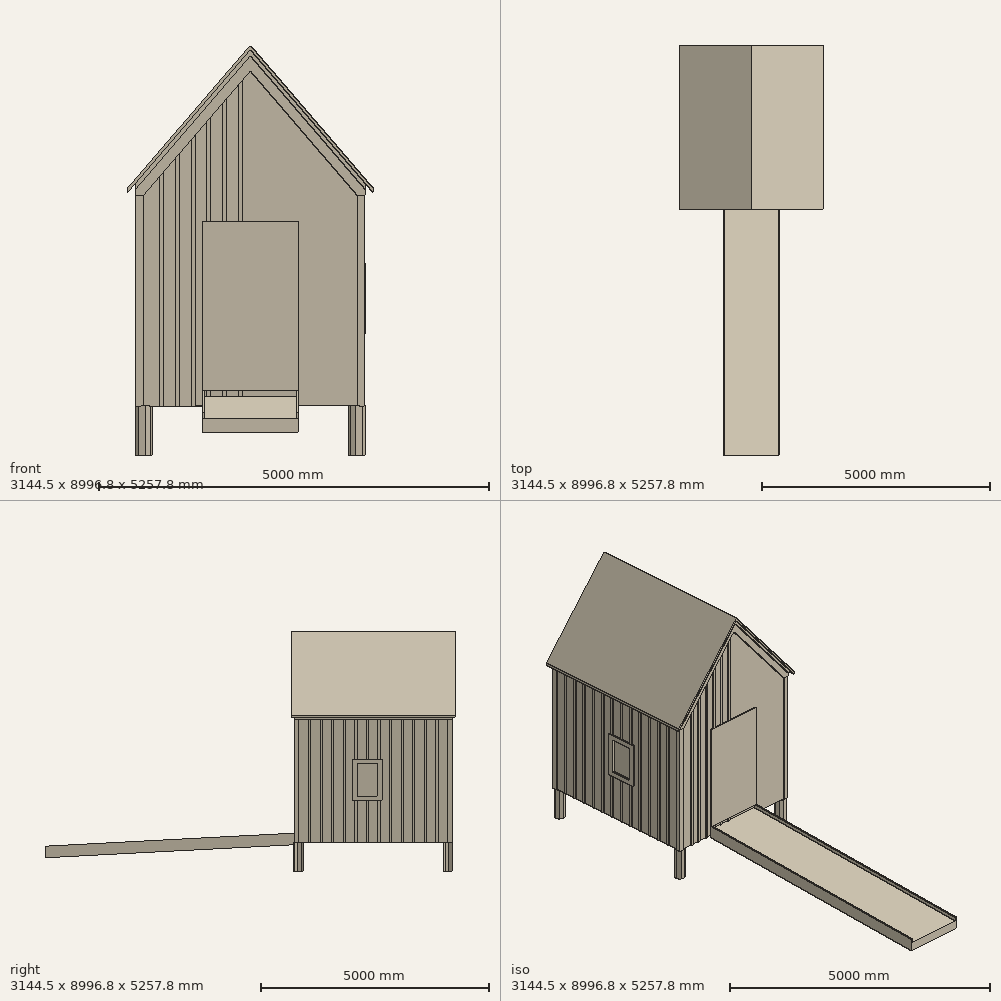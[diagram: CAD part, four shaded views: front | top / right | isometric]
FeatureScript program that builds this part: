
annotation { "Feature Type Name" : "Feature", "Feature Type Description" : "" }
export const myFeature = defineFeature(function(context is Context, id is Id, definition is map)
    precondition{}
    {
        {
            var Q0;
            Q0=qCreatedBy(makeId("Front.planeOp"),FACE);
            var sketch = newSketch(context, id + "F0", { "sketchPlane" : qUnion([Q0])});
            skLineSegment(sketch, "E0", {"start": v(0, 0) * mm, "end": v(0, 2794) * mm});
            skLineSegment(sketch, "E1", {"start": v(0, 2794) * mm, "end": v(1572.26, 4622.8) * mm});
            skLineSegment(sketch, "E2", {"start": v(1572.26, 4622.8) * mm, "end": v(3144.52, 2794) * mm});
            skLineSegment(sketch, "E3", {"start": v(3144.52, 2794) * mm, "end": v(3144.52, 0) * mm});
            skLineSegment(sketch, "E4", {"start": v(3144.52, 0) * mm, "end": v(0, 0) * mm});
            skSolve(sketch);
        }
        {
            var Q0;
            Q0 = qSketchRegion(id + "F0", true);
            extrude(context, id + "F1", {"entities" : qUnion([Q0]), "oppositeDirection" : true, "depth" : 3606.8 * mm});
        }
        {
            var Q0;
            Q0=makeQuery(id+"F1.opExtrude","CAP_FACE",FACE,{"disambiguationData":[OSD([sQuery(id+"F0.wireOp",EDGE,"E0"),sQuery(id+"F0.wireOp",EDGE,"E1"),sQuery(id+"F0.wireOp",EDGE,"E2"),sQuery(id+"F0.wireOp",EDGE,"E3"),sQuery(id+"F0.wireOp",EDGE,"E4")])],"isStart":true});
            var sketch = newSketch(context, id + "F2", { "sketchPlane" : qUnion([Q0])});
            skLineSegment(sketch, "E5", {"start": v(1572.26, 4622.8) * mm, "end": v(1572.26, 2444.29) * mm, "construction": true});
            skLineSegment(sketch, "E6", {"start": v(101.6, 2853.73) * mm, "end": v(101.6, 2701.33) * mm});
            skLineSegment(sketch, "E7", {"start": v(101.6, 2701.33) * mm, "end": v(127, 2701.33) * mm});
            skLineSegment(sketch, "E8", {"start": v(127, 2701.33) * mm, "end": v(127, 0) * mm});
            skPoint(sketch, "E9.orphan", {"position": v(101.6, 0) * mm});
            skLineSegment(sketch, "E10", {"start": v(101.6, 2853.73) * mm, "end": v(0, 2735.56) * mm});
            skLineSegment(sketch, "E11.MirrorCS", {"start": v(3042.92, 2701.33) * mm, "end": v(3017.52, 2701.33) * mm});
            skLineSegment(sketch, "E12.MirrorCS", {"start": v(3042.92, 2853.73) * mm, "end": v(3042.92, 2701.33) * mm});
            skLineSegment(sketch, "E13.MirrorCS", {"start": v(3042.92, 2853.73) * mm, "end": v(3144.52, 2735.56) * mm});
            skLineSegment(sketch, "E14.MirrorCS", {"start": v(3017.52, 2701.33) * mm, "end": v(3017.52, 0) * mm});
            skPoint(sketch, "E15.MirrorP", {"position": v(3042.92, 0) * mm});
            skSolve(sketch);
        }
        {
            var Q0;
            Q0=makeQuery(id+"F2.imprint","IMPRINT",FACE,{"disambiguationData":[TD([[makeQuery(id+"F2.imprint","IMPRINT",EDGE,{"derivedFrom":sQuery(id+"F2.wireOp",EDGE,"E6")}),-1.0]])]});
            var Q1;
            Q1=makeQuery(id+"F2.imprint","IMPRINT",FACE,{"disambiguationData":[TD([[makeQuery(id+"F2.imprint","IMPRINT",EDGE,{"derivedFrom":sQuery(id+"F2.wireOp",EDGE,"E11.MirrorCS")}),1.0]])]});
            extrude(context, id + "F3", {"entities" : qUnion([Q0, Q1]), "operationType" : NewBodyOperationType.REMOVE, "endBound" : BoundingType.THROUGH_ALL, "oppositeDirection" : true, "depth" : 25.4 * mm});
        }
        {
            var Q0;
            Q0=makeQuery(id+"F1.opExtrude","CAP_FACE",FACE,{"disambiguationData":[OSD([sQuery(id+"F0.wireOp",EDGE,"E0"),sQuery(id+"F0.wireOp",EDGE,"E1"),sQuery(id+"F0.wireOp",EDGE,"E2"),sQuery(id+"F0.wireOp",EDGE,"E3"),sQuery(id+"F0.wireOp",EDGE,"E4")])],"isStart":true});
            var sketch = newSketch(context, id + "F4", { "sketchPlane" : qUnion([Q0])});
            skLineSegment(sketch, "E16", {"start": v(101.6, 2853.73) * mm, "end": v(1572.26, 4564.36) * mm});
            skLineSegment(sketch, "E17", {"start": v(1572.26, 4564.36) * mm, "end": v(3042.92, 2853.73) * mm});
            skSolve(sketch);
        }
        {
            var Q0;
            Q0=makeQuery(id+"F4.imprint","IMPRINT",FACE,{"disambiguationData":[TD([[makeQuery(id+"F4.imprint","IMPRINT",EDGE,{"derivedFrom":sQuery(id+"F4.wireOp",EDGE,"E16")}),-1.0]])]});
            extrude(context, id + "F5", {"entities" : qUnion([Q0]), "operationType" : NewBodyOperationType.REMOVE, "oppositeDirection" : true, "depth" : 25.4 * mm});
        }
        {
            var Q0;
            Q0=makeQuery(id+"F1.opExtrude","CAP_FACE",FACE,{"disambiguationData":[OSD([sQuery(id+"F0.wireOp",EDGE,"E0"),sQuery(id+"F0.wireOp",EDGE,"E1"),sQuery(id+"F0.wireOp",EDGE,"E2"),sQuery(id+"F0.wireOp",EDGE,"E3"),sQuery(id+"F0.wireOp",EDGE,"E4")])],"isStart":false});
            var sketch = newSketch(context, id + "F6", { "sketchPlane" : qUnion([Q0])});
            skLineSegment(sketch, "E18.0.0", {"start": v(-1572.26, 4564.36) * mm, "end": v(-101.6, 2853.73) * mm});
            skLineSegment(sketch, "E18.0.1", {"start": v(-101.6, 2853.73) * mm, "end": v(-101.6, 2701.33) * mm});
            skLineSegment(sketch, "E18.0.2", {"start": v(-101.6, 2701.33) * mm, "end": v(-127, 2701.33) * mm});
            skLineSegment(sketch, "E18.0.3", {"start": v(-127, 2701.33) * mm, "end": v(-127, 0) * mm});
            skLineSegment(sketch, "E18.0.4", {"start": v(-127, 0) * mm, "end": v(-3017.52, 0) * mm});
            skLineSegment(sketch, "E18.0.5", {"start": v(-3017.52, 0) * mm, "end": v(-3017.52, 2701.33) * mm});
            skLineSegment(sketch, "E18.0.6", {"start": v(-3017.52, 2701.33) * mm, "end": v(-3042.92, 2701.33) * mm});
            skLineSegment(sketch, "E18.0.7", {"start": v(-3042.92, 2701.33) * mm, "end": v(-3042.92, 2853.73) * mm});
            skLineSegment(sketch, "E18.0.8", {"start": v(-3042.92, 2853.73) * mm, "end": v(-1572.26, 4564.36) * mm});
            skSolve(sketch);
        }
        {
            var Q0;
            Q0 = qSketchRegion(id + "F6", true);
            extrude(context, id + "F7", {"entities" : qUnion([Q0]), "operationType" : NewBodyOperationType.REMOVE, "oppositeDirection" : true, "depth" : 25.4 * mm});
        }
        {
            var Q0;
            Q0=makeQuery(id+"F5.boolean.opBoolean","COPY",FACE,{"derivedFrom":makeQuery(id+"F5.opExtrude","CAP_FACE",FACE,{"disambiguationData":[OSD([sQuery(id+"F0.wireOp",EDGE,"E4"),sQuery(id+"F2.wireOp",EDGE,"E6"),sQuery(id+"F2.wireOp",EDGE,"E7"),sQuery(id+"F2.wireOp",EDGE,"E8"),sQuery(id+"F2.wireOp",EDGE,"E11.MirrorCS"),sQuery(id+"F2.wireOp",EDGE,"E12.MirrorCS"),sQuery(id+"F2.wireOp",EDGE,"E14.MirrorCS"),sQuery(id+"F4.wireOp",EDGE,"E16"),sQuery(id+"F4.wireOp",EDGE,"E17")])],"isStart":false})});
            var sketch = newSketch(context, id + "F8", { "sketchPlane" : qUnion([Q0])});
            skLineSegment(sketch, "E19", {"start": v(101.6, 2775.81) * mm, "end": v(1572.26, 4486.43) * mm});
            skLineSegment(sketch, "E20", {"start": v(1572.26, 4486.43) * mm, "end": v(3042.92, 2775.81) * mm});
            skSolve(sketch);
        }
        {
            var Q0;
            {var subQ3=sQuery(id+"F8.wireOp",EDGE,"E19");Q0=makeQuery(id+"F8.imprint","IMPRINT",FACE,{"disambiguationData":[TD([[makeQuery(id+"F8.imprint","IMPRINT",EDGE,{"derivedFrom":subQ3}),-1.0]])]});}
            extrude(context, id + "F9", {"entities" : qUnion([Q0]), "operationType" : NewBodyOperationType.REMOVE, "oppositeDirection" : true, "depth" : 38.1 * mm});
        }
        {
            var Q0;
            Q0=makeQuery(id+"F7.boolean.opBoolean","COPY",FACE,{"derivedFrom":makeQuery(id+"F7.opExtrude","CAP_FACE",FACE,{"disambiguationData":[OSD([sQuery(id+"F6.wireOp",EDGE,"E18.0.0"),sQuery(id+"F6.wireOp",EDGE,"E18.0.1"),sQuery(id+"F6.wireOp",EDGE,"E18.0.2"),sQuery(id+"F6.wireOp",EDGE,"E18.0.3"),sQuery(id+"F6.wireOp",EDGE,"E18.0.4"),sQuery(id+"F6.wireOp",EDGE,"E18.0.5"),sQuery(id+"F6.wireOp",EDGE,"E18.0.6"),sQuery(id+"F6.wireOp",EDGE,"E18.0.7"),sQuery(id+"F6.wireOp",EDGE,"E18.0.8")])],"isStart":false})});
            var sketch = newSketch(context, id + "F10", { "sketchPlane" : qUnion([Q0])});
            skLineSegment(sketch, "E21.0.0", {"start": v(-1572.26, 4486.43) * mm, "end": v(-101.6, 2775.81) * mm});
            skLineSegment(sketch, "E21.0.1", {"start": v(-101.6, 2775.81) * mm, "end": v(-101.6, 2701.33) * mm});
            skLineSegment(sketch, "E21.0.2", {"start": v(-101.6, 2701.33) * mm, "end": v(-127, 2701.33) * mm});
            skLineSegment(sketch, "E21.0.3", {"start": v(-127, 2701.33) * mm, "end": v(-127, 0) * mm});
            skLineSegment(sketch, "E21.0.4", {"start": v(-127, 0) * mm, "end": v(-3017.52, 0) * mm});
            skLineSegment(sketch, "E21.0.5", {"start": v(-3017.52, 0) * mm, "end": v(-3017.52, 2701.33) * mm});
            skLineSegment(sketch, "E21.0.6", {"start": v(-3017.52, 2701.33) * mm, "end": v(-3042.92, 2701.33) * mm});
            skLineSegment(sketch, "E21.0.7", {"start": v(-3042.92, 2701.33) * mm, "end": v(-3042.92, 2775.81) * mm});
            skLineSegment(sketch, "E21.0.8", {"start": v(-3042.92, 2775.81) * mm, "end": v(-1572.26, 4486.43) * mm});
            skSolve(sketch);
        }
        {
            var Q0;
            Q0 = qSketchRegion(id + "F10", true);
            extrude(context, id + "F11", {"entities" : qUnion([Q0]), "operationType" : NewBodyOperationType.REMOVE, "oppositeDirection" : true, "depth" : 38.1 * mm});
        }
        {
            var Q0;
            Q0=makeQuery(id+"F9.boolean.opBoolean","COPY",FACE,{"derivedFrom":makeQuery(id+"F9.opExtrude","CAP_FACE",FACE,{"disambiguationData":[OSD([sQuery(id+"F0.wireOp",EDGE,"E4"),sQuery(id+"F2.wireOp",EDGE,"E6"),sQuery(id+"F2.wireOp",EDGE,"E7"),sQuery(id+"F2.wireOp",EDGE,"E8"),sQuery(id+"F2.wireOp",EDGE,"E11.MirrorCS"),sQuery(id+"F2.wireOp",EDGE,"E12.MirrorCS"),sQuery(id+"F2.wireOp",EDGE,"E14.MirrorCS"),sQuery(id+"F8.wireOp",EDGE,"E19"),sQuery(id+"F8.wireOp",EDGE,"E20")])],"isStart":false})});
            var sketch = newSketch(context, id + "F12", { "sketchPlane" : qUnion([Q0])});
            skLineSegment(sketch, "E22", {"start": v(127, 2701.33) * mm, "end": v(205.05, 2701.33) * mm});
            skLineSegment(sketch, "E23", {"start": v(205.05, 2701.33) * mm, "end": v(1572.26, 4291.62) * mm});
            skLineSegment(sketch, "E24", {"start": v(1572.26, 4291.62) * mm, "end": v(2939.47, 2701.33) * mm});
            skLineSegment(sketch, "E25", {"start": v(2939.47, 2701.33) * mm, "end": v(3017.52, 2701.33) * mm});
            skSolve(sketch);
        }
        {
            var Q0;
            Q0=makeQuery(id+"F12.imprint","IMPRINT",FACE,{"disambiguationData":[TD([[makeQuery(id+"F12.imprint","IMPRINT",EDGE,{"derivedFrom":sQuery(id+"F12.wireOp",EDGE,"E22")}),-1.0]])]});
            extrude(context, id + "F13", {"entities" : qUnion([Q0]), "operationType" : NewBodyOperationType.REMOVE, "oppositeDirection" : true, "depth" : 25.4 * mm});
        }
        {
            var Q0;
            Q0=makeQuery(id+"F11.boolean.opBoolean","COPY",FACE,{"derivedFrom":makeQuery(id+"F11.opExtrude","CAP_FACE",FACE,{"disambiguationData":[OSD([sQuery(id+"F10.wireOp",EDGE,"E21.0.0"),sQuery(id+"F10.wireOp",EDGE,"E21.0.1"),sQuery(id+"F10.wireOp",EDGE,"E21.0.2"),sQuery(id+"F10.wireOp",EDGE,"E21.0.3"),sQuery(id+"F10.wireOp",EDGE,"E21.0.4"),sQuery(id+"F10.wireOp",EDGE,"E21.0.5"),sQuery(id+"F10.wireOp",EDGE,"E21.0.6"),sQuery(id+"F10.wireOp",EDGE,"E21.0.7"),sQuery(id+"F10.wireOp",EDGE,"E21.0.8")])],"isStart":false})});
            var sketch = newSketch(context, id + "F14", { "sketchPlane" : qUnion([Q0])});
            skLineSegment(sketch, "E26.0.0", {"start": v(-205.05, 2701.33) * mm, "end": v(-127, 2701.33) * mm});
            skLineSegment(sketch, "E26.0.1", {"start": v(-127, 2701.33) * mm, "end": v(-127, 0) * mm});
            skLineSegment(sketch, "E26.0.2", {"start": v(-127, 0) * mm, "end": v(-3017.52, 0) * mm});
            skLineSegment(sketch, "E26.0.3", {"start": v(-3017.52, 0) * mm, "end": v(-3017.52, 2701.33) * mm});
            skLineSegment(sketch, "E26.0.4", {"start": v(-3017.52, 2701.33) * mm, "end": v(-2939.47, 2701.33) * mm});
            skLineSegment(sketch, "E26.0.5", {"start": v(-2939.47, 2701.33) * mm, "end": v(-1572.26, 4291.62) * mm});
            skLineSegment(sketch, "E26.0.6", {"start": v(-1572.26, 4291.62) * mm, "end": v(-205.05, 2701.33) * mm});
            skSolve(sketch);
        }
        {
            var Q0;
            Q0 = qSketchRegion(id + "F14", true);
            extrude(context, id + "F15", {"entities" : qUnion([Q0]), "operationType" : NewBodyOperationType.REMOVE, "oppositeDirection" : true, "depth" : 25.4 * mm});
        }
        {
            var Q0;
            Q0=makeQuery(id+"F1.opExtrude","SWEPT_FACE",FACE,{"disambiguationData":[OSD([sQuery(id+"F0.wireOp",EDGE,"E4")])]});
            var sketch = newSketch(context, id + "F16", { "sketchPlane" : qUnion([Q0])});
            skLineSegment(sketch, "E27.bottom", {"start": v(99.06, -66.04) * mm, "end": v(200.66, -66.04) * mm});
            skLineSegment(sketch, "E27.top", {"start": v(99.06, -167.64) * mm, "end": v(200.66, -167.64) * mm});
            skLineSegment(sketch, "E27.left", {"start": v(99.06, -66.04) * mm, "end": v(99.06, -167.64) * mm});
            skLineSegment(sketch, "E27.right", {"start": v(200.66, -66.04) * mm, "end": v(200.66, -167.64) * mm});
            skLineSegment(sketch, "E28.bottom", {"start": v(99.06, -3540.76) * mm, "end": v(200.66, -3540.76) * mm});
            skLineSegment(sketch, "E28.top", {"start": v(99.06, -3439.16) * mm, "end": v(200.66, -3439.16) * mm});
            skLineSegment(sketch, "E28.left", {"start": v(99.06, -3540.76) * mm, "end": v(99.06, -3439.16) * mm});
            skLineSegment(sketch, "E28.right", {"start": v(200.66, -3540.76) * mm, "end": v(200.66, -3439.16) * mm});
            skLineSegment(sketch, "E29.bottom", {"start": v(3040.38, -3540.76) * mm, "end": v(2938.78, -3540.76) * mm});
            skLineSegment(sketch, "E29.top", {"start": v(3040.38, -3439.16) * mm, "end": v(2938.78, -3439.16) * mm});
            skLineSegment(sketch, "E29.left", {"start": v(3040.38, -3540.76) * mm, "end": v(3040.38, -3439.16) * mm});
            skLineSegment(sketch, "E29.right", {"start": v(2938.78, -3540.76) * mm, "end": v(2938.78, -3439.16) * mm});
            skLineSegment(sketch, "E30.bottom", {"start": v(3040.38, -66.04) * mm, "end": v(2938.78, -66.04) * mm});
            skLineSegment(sketch, "E30.top", {"start": v(3040.38, -167.64) * mm, "end": v(2938.78, -167.64) * mm});
            skLineSegment(sketch, "E30.left", {"start": v(3040.38, -66.04) * mm, "end": v(3040.38, -167.64) * mm});
            skLineSegment(sketch, "E30.right", {"start": v(2938.78, -66.04) * mm, "end": v(2938.78, -167.64) * mm});
            skSolve(sketch);
        }
        {
            var Q0;
            Q0 = qSketchRegion(id + "F16", true);
            var Q1;
            Q1=makeQuery(id+"F15.boolean.opBoolean","MERGE",FACE,{"derivedFrom":[makeQuery(id+"F13.boolean.opBoolean","MERGE",FACE,{"derivedFrom":[makeQuery(id+"F3.boolean.opBoolean","COPY",FACE,{"derivedFrom":makeQuery(id+"F3.opExtrude","SWEPT_FACE",FACE,{"disambiguationData":[OSD([sQuery(id+"F2.wireOp",EDGE,"E11.MirrorCS")])]})}),makeQuery(id+"F13.opExtrude","SWEPT_FACE",FACE,{"disambiguationData":[OSD([sQuery(id+"F12.wireOp",EDGE,"E25")])]})]}),makeQuery(id+"F15.opExtrude","SWEPT_FACE",FACE,{"disambiguationData":[OSD([sQuery(id+"F14.wireOp",EDGE,"E26.0.4")])]})]});
            extrude(context, id + "F17", {"entities" : qUnion([Q0]), "operationType" : NewBodyOperationType.ADD, "endBound" : BoundingType.UP_TO_SURFACE, "oppositeDirection" : true, "endBoundEntityFace" : qUnion([Q1]), "depth" : 25.4 * mm});
        }
        {
            var Q0;
            Q0=makeQuery(id+"F17.boolean.opBoolean","MERGE",FACE,{"derivedFrom":[makeQuery(id+"F1.opExtrude","SWEPT_FACE",FACE,{"disambiguationData":[OSD([sQuery(id+"F0.wireOp",EDGE,"E4")])]}),makeQuery(id+"F17.opExtrude","CAP_FACE",FACE,{"disambiguationData":[OSD([sQuery(id+"F16.wireOp",EDGE,"E27.bottom"),sQuery(id+"F16.wireOp",EDGE,"E27.top"),sQuery(id+"F16.wireOp",EDGE,"E27.left"),sQuery(id+"F16.wireOp",EDGE,"E27.right")])],"isStart":true}),makeQuery(id+"F17.opExtrude","CAP_FACE",FACE,{"disambiguationData":[OSD([sQuery(id+"F16.wireOp",EDGE,"E28.bottom"),sQuery(id+"F16.wireOp",EDGE,"E28.top"),sQuery(id+"F16.wireOp",EDGE,"E28.left"),sQuery(id+"F16.wireOp",EDGE,"E28.right")])],"isStart":true}),makeQuery(id+"F17.opExtrude","CAP_FACE",FACE,{"disambiguationData":[OSD([sQuery(id+"F16.wireOp",EDGE,"E29.bottom"),sQuery(id+"F16.wireOp",EDGE,"E29.top"),sQuery(id+"F16.wireOp",EDGE,"E29.left"),sQuery(id+"F16.wireOp",EDGE,"E29.right")])],"isStart":true}),makeQuery(id+"F17.opExtrude","CAP_FACE",FACE,{"disambiguationData":[OSD([sQuery(id+"F16.wireOp",EDGE,"E30.bottom"),sQuery(id+"F16.wireOp",EDGE,"E30.top"),sQuery(id+"F16.wireOp",EDGE,"E30.left"),sQuery(id+"F16.wireOp",EDGE,"E30.right")])],"isStart":true})]});
            var sketch = newSketch(context, id + "F18", { "sketchPlane" : qUnion([Q0])});
            skLineSegment(sketch, "E31.bottom", {"start": v(104.14, -3175) * mm, "end": v(127, -3175) * mm});
            skLineSegment(sketch, "E31.top", {"start": v(104.14, -3225.8) * mm, "end": v(127, -3225.8) * mm});
            skLineSegment(sketch, "E31.left", {"start": v(104.14, -3175) * mm, "end": v(104.14, -3225.8) * mm});
            skLineSegment(sketch, "E31.right", {"start": v(127, -3175) * mm, "end": v(127, -3225.8) * mm});
            skLineSegment(sketch, "E32.0.1.0", {"start": v(104.14, -2971.8) * mm, "end": v(127, -2971.8) * mm});
            skLineSegment(sketch, "E32.0.1.1", {"start": v(127, -2921) * mm, "end": v(127, -2971.8) * mm});
            skLineSegment(sketch, "E32.0.1.2", {"start": v(104.14, -2921) * mm, "end": v(127, -2921) * mm});
            skLineSegment(sketch, "E32.0.1.3", {"start": v(104.14, -2921) * mm, "end": v(104.14, -2971.8) * mm});
            skLineSegment(sketch, "E32.0.2.0", {"start": v(104.14, -2717.8) * mm, "end": v(127, -2717.8) * mm});
            skLineSegment(sketch, "E32.0.2.1", {"start": v(127, -2667) * mm, "end": v(127, -2717.8) * mm});
            skLineSegment(sketch, "E32.0.2.2", {"start": v(104.14, -2667) * mm, "end": v(127, -2667) * mm});
            skLineSegment(sketch, "E32.0.2.3", {"start": v(104.14, -2667) * mm, "end": v(104.14, -2717.8) * mm});
            skLineSegment(sketch, "E32.0.3.0", {"start": v(104.14, -2463.8) * mm, "end": v(127, -2463.8) * mm});
            skLineSegment(sketch, "E32.0.3.1", {"start": v(127, -2413) * mm, "end": v(127, -2463.8) * mm});
            skLineSegment(sketch, "E32.0.3.2", {"start": v(104.14, -2413) * mm, "end": v(127, -2413) * mm});
            skLineSegment(sketch, "E32.0.3.3", {"start": v(104.14, -2413) * mm, "end": v(104.14, -2463.8) * mm});
            skLineSegment(sketch, "E32.0.4.0", {"start": v(104.14, -2209.8) * mm, "end": v(127, -2209.8) * mm});
            skLineSegment(sketch, "E32.0.4.1", {"start": v(127, -2159) * mm, "end": v(127, -2209.8) * mm});
            skLineSegment(sketch, "E32.0.4.2", {"start": v(104.14, -2159) * mm, "end": v(127, -2159) * mm});
            skLineSegment(sketch, "E32.0.4.3", {"start": v(104.14, -2159) * mm, "end": v(104.14, -2209.8) * mm});
            skLineSegment(sketch, "E32.0.5.0", {"start": v(104.14, -1955.8) * mm, "end": v(127, -1955.8) * mm});
            skLineSegment(sketch, "E32.0.5.1", {"start": v(127, -1905) * mm, "end": v(127, -1955.8) * mm});
            skLineSegment(sketch, "E32.0.5.2", {"start": v(104.14, -1905) * mm, "end": v(127, -1905) * mm});
            skLineSegment(sketch, "E32.0.5.3", {"start": v(104.14, -1905) * mm, "end": v(104.14, -1955.8) * mm});
            skLineSegment(sketch, "E32.0.6.0", {"start": v(104.14, -1701.8) * mm, "end": v(127, -1701.8) * mm});
            skLineSegment(sketch, "E32.0.6.1", {"start": v(127, -1651) * mm, "end": v(127, -1701.8) * mm});
            skLineSegment(sketch, "E32.0.6.2", {"start": v(104.14, -1651) * mm, "end": v(127, -1651) * mm});
            skLineSegment(sketch, "E32.0.6.3", {"start": v(104.14, -1651) * mm, "end": v(104.14, -1701.8) * mm});
            skLineSegment(sketch, "E32.0.7.0", {"start": v(104.14, -1447.8) * mm, "end": v(127, -1447.8) * mm});
            skLineSegment(sketch, "E32.0.7.1", {"start": v(127, -1397) * mm, "end": v(127, -1447.8) * mm});
            skLineSegment(sketch, "E32.0.7.2", {"start": v(104.14, -1397) * mm, "end": v(127, -1397) * mm});
            skLineSegment(sketch, "E32.0.7.3", {"start": v(104.14, -1397) * mm, "end": v(104.14, -1447.8) * mm});
            skLineSegment(sketch, "E32.0.8.0", {"start": v(104.14, -1193.8) * mm, "end": v(127, -1193.8) * mm});
            skLineSegment(sketch, "E32.0.8.1", {"start": v(127, -1143) * mm, "end": v(127, -1193.8) * mm});
            skLineSegment(sketch, "E32.0.8.2", {"start": v(104.14, -1143) * mm, "end": v(127, -1143) * mm});
            skLineSegment(sketch, "E32.0.8.3", {"start": v(104.14, -1143) * mm, "end": v(104.14, -1193.8) * mm});
            skLineSegment(sketch, "E32.0.9.0", {"start": v(104.14, -939.8) * mm, "end": v(127, -939.8) * mm});
            skLineSegment(sketch, "E32.0.9.1", {"start": v(127, -889) * mm, "end": v(127, -939.8) * mm});
            skLineSegment(sketch, "E32.0.9.2", {"start": v(104.14, -889) * mm, "end": v(127, -889) * mm});
            skLineSegment(sketch, "E32.0.9.3", {"start": v(104.14, -889) * mm, "end": v(104.14, -939.8) * mm});
            skLineSegment(sketch, "E32.0.10.0", {"start": v(104.14, -685.8) * mm, "end": v(127, -685.8) * mm});
            skLineSegment(sketch, "E32.0.10.1", {"start": v(127, -635) * mm, "end": v(127, -685.8) * mm});
            skLineSegment(sketch, "E32.0.10.2", {"start": v(104.14, -635) * mm, "end": v(127, -635) * mm});
            skLineSegment(sketch, "E32.0.10.3", {"start": v(104.14, -635) * mm, "end": v(104.14, -685.8) * mm});
            skLineSegment(sketch, "E32.0.11.0", {"start": v(104.14, -431.8) * mm, "end": v(127, -431.8) * mm});
            skLineSegment(sketch, "E32.0.11.1", {"start": v(127, -381) * mm, "end": v(127, -431.8) * mm});
            skLineSegment(sketch, "E32.0.11.2", {"start": v(104.14, -381) * mm, "end": v(127, -381) * mm});
            skLineSegment(sketch, "E32.0.11.3", {"start": v(104.14, -381) * mm, "end": v(104.14, -431.8) * mm});
            skLineSegment(sketch, "E32.1.0.0", {"start": v(3017.52, -3225.8) * mm, "end": v(3040.38, -3225.8) * mm});
            skLineSegment(sketch, "E32.1.0.1", {"start": v(3040.38, -3175) * mm, "end": v(3040.38, -3225.8) * mm});
            skLineSegment(sketch, "E32.1.0.2", {"start": v(3017.52, -3175) * mm, "end": v(3040.38, -3175) * mm});
            skLineSegment(sketch, "E32.1.0.3", {"start": v(3017.52, -3175) * mm, "end": v(3017.52, -3225.8) * mm});
            skLineSegment(sketch, "E32.1.1.0", {"start": v(3017.52, -2971.8) * mm, "end": v(3040.38, -2971.8) * mm});
            skLineSegment(sketch, "E32.1.1.1", {"start": v(3040.38, -2921) * mm, "end": v(3040.38, -2971.8) * mm});
            skLineSegment(sketch, "E32.1.1.2", {"start": v(3017.52, -2921) * mm, "end": v(3040.38, -2921) * mm});
            skLineSegment(sketch, "E32.1.1.3", {"start": v(3017.52, -2921) * mm, "end": v(3017.52, -2971.8) * mm});
            skLineSegment(sketch, "E32.1.2.0", {"start": v(3017.52, -2717.8) * mm, "end": v(3040.38, -2717.8) * mm});
            skLineSegment(sketch, "E32.1.2.1", {"start": v(3040.38, -2667) * mm, "end": v(3040.38, -2717.8) * mm});
            skLineSegment(sketch, "E32.1.2.2", {"start": v(3017.52, -2667) * mm, "end": v(3040.38, -2667) * mm});
            skLineSegment(sketch, "E32.1.2.3", {"start": v(3017.52, -2667) * mm, "end": v(3017.52, -2717.8) * mm});
            skLineSegment(sketch, "E32.1.3.0", {"start": v(3017.52, -2463.8) * mm, "end": v(3040.38, -2463.8) * mm});
            skLineSegment(sketch, "E32.1.3.1", {"start": v(3040.38, -2413) * mm, "end": v(3040.38, -2463.8) * mm});
            skLineSegment(sketch, "E32.1.3.2", {"start": v(3017.52, -2413) * mm, "end": v(3040.38, -2413) * mm});
            skLineSegment(sketch, "E32.1.3.3", {"start": v(3017.52, -2413) * mm, "end": v(3017.52, -2463.8) * mm});
            skLineSegment(sketch, "E32.1.4.0", {"start": v(3017.52, -2209.8) * mm, "end": v(3040.38, -2209.8) * mm});
            skLineSegment(sketch, "E32.1.4.1", {"start": v(3040.38, -2159) * mm, "end": v(3040.38, -2209.8) * mm});
            skLineSegment(sketch, "E32.1.4.2", {"start": v(3017.52, -2159) * mm, "end": v(3040.38, -2159) * mm});
            skLineSegment(sketch, "E32.1.4.3", {"start": v(3017.52, -2159) * mm, "end": v(3017.52, -2209.8) * mm});
            skLineSegment(sketch, "E32.1.5.0", {"start": v(3017.52, -1955.8) * mm, "end": v(3040.38, -1955.8) * mm});
            skLineSegment(sketch, "E32.1.5.1", {"start": v(3040.38, -1905) * mm, "end": v(3040.38, -1955.8) * mm});
            skLineSegment(sketch, "E32.1.5.2", {"start": v(3017.52, -1905) * mm, "end": v(3040.38, -1905) * mm});
            skLineSegment(sketch, "E32.1.5.3", {"start": v(3017.52, -1905) * mm, "end": v(3017.52, -1955.8) * mm});
            skLineSegment(sketch, "E32.1.6.0", {"start": v(3017.52, -1701.8) * mm, "end": v(3040.38, -1701.8) * mm});
            skLineSegment(sketch, "E32.1.6.1", {"start": v(3040.38, -1651) * mm, "end": v(3040.38, -1701.8) * mm});
            skLineSegment(sketch, "E32.1.6.2", {"start": v(3017.52, -1651) * mm, "end": v(3040.38, -1651) * mm});
            skLineSegment(sketch, "E32.1.6.3", {"start": v(3017.52, -1651) * mm, "end": v(3017.52, -1701.8) * mm});
            skLineSegment(sketch, "E32.1.7.0", {"start": v(3017.52, -1447.8) * mm, "end": v(3040.38, -1447.8) * mm});
            skLineSegment(sketch, "E32.1.7.1", {"start": v(3040.38, -1397) * mm, "end": v(3040.38, -1447.8) * mm});
            skLineSegment(sketch, "E32.1.7.2", {"start": v(3017.52, -1397) * mm, "end": v(3040.38, -1397) * mm});
            skLineSegment(sketch, "E32.1.7.3", {"start": v(3017.52, -1397) * mm, "end": v(3017.52, -1447.8) * mm});
            skLineSegment(sketch, "E32.1.8.0", {"start": v(3017.52, -1193.8) * mm, "end": v(3040.38, -1193.8) * mm});
            skLineSegment(sketch, "E32.1.8.1", {"start": v(3040.38, -1143) * mm, "end": v(3040.38, -1193.8) * mm});
            skLineSegment(sketch, "E32.1.8.2", {"start": v(3017.52, -1143) * mm, "end": v(3040.38, -1143) * mm});
            skLineSegment(sketch, "E32.1.8.3", {"start": v(3017.52, -1143) * mm, "end": v(3017.52, -1193.8) * mm});
            skLineSegment(sketch, "E32.1.9.0", {"start": v(3017.52, -939.8) * mm, "end": v(3040.38, -939.8) * mm});
            skLineSegment(sketch, "E32.1.9.1", {"start": v(3040.38, -889) * mm, "end": v(3040.38, -939.8) * mm});
            skLineSegment(sketch, "E32.1.9.2", {"start": v(3017.52, -889) * mm, "end": v(3040.38, -889) * mm});
            skLineSegment(sketch, "E32.1.9.3", {"start": v(3017.52, -889) * mm, "end": v(3017.52, -939.8) * mm});
            skLineSegment(sketch, "E32.1.10.0", {"start": v(3017.52, -685.8) * mm, "end": v(3040.38, -685.8) * mm});
            skLineSegment(sketch, "E32.1.10.1", {"start": v(3040.38, -635) * mm, "end": v(3040.38, -685.8) * mm});
            skLineSegment(sketch, "E32.1.10.2", {"start": v(3017.52, -635) * mm, "end": v(3040.38, -635) * mm});
            skLineSegment(sketch, "E32.1.10.3", {"start": v(3017.52, -635) * mm, "end": v(3017.52, -685.8) * mm});
            skLineSegment(sketch, "E32.1.11.0", {"start": v(3017.52, -431.8) * mm, "end": v(3040.38, -431.8) * mm});
            skLineSegment(sketch, "E32.1.11.1", {"start": v(3040.38, -381) * mm, "end": v(3040.38, -431.8) * mm});
            skLineSegment(sketch, "E32.1.11.2", {"start": v(3017.52, -381) * mm, "end": v(3040.38, -381) * mm});
            skLineSegment(sketch, "E32.1.11.3", {"start": v(3017.52, -381) * mm, "end": v(3017.52, -431.8) * mm});
            skLineSegment(sketch, "E32.direction1", {"start": v(104.14, -3225.8) * mm, "end": v(3017.52, -3225.8) * mm, "construction": true});
            skLineSegment(sketch, "E32.direction2", {"start": v(104.14, -3225.8) * mm, "end": v(104.14, -2971.8) * mm, "construction": true});
            skSolve(sketch);
        }
        {
            var Q0;
            Q0 = qSketchRegion(id + "F18", true);
            var Q1;
            Q1=makeQuery(id+"F15.boolean.opBoolean","MERGE",FACE,{"derivedFrom":[makeQuery(id+"F13.boolean.opBoolean","MERGE",FACE,{"derivedFrom":[makeQuery(id+"F3.boolean.opBoolean","COPY",FACE,{"derivedFrom":makeQuery(id+"F3.opExtrude","SWEPT_FACE",FACE,{"disambiguationData":[OSD([sQuery(id+"F2.wireOp",EDGE,"E11.MirrorCS")])]})}),makeQuery(id+"F13.opExtrude","SWEPT_FACE",FACE,{"disambiguationData":[OSD([sQuery(id+"F12.wireOp",EDGE,"E25")])]})]}),makeQuery(id+"F15.opExtrude","SWEPT_FACE",FACE,{"disambiguationData":[OSD([sQuery(id+"F14.wireOp",EDGE,"E26.0.4")])]})]});
            extrude(context, id + "F19", {"entities" : qUnion([Q0]), "operationType" : NewBodyOperationType.ADD, "endBound" : BoundingType.UP_TO_SURFACE, "oppositeDirection" : true, "endBoundEntityFace" : qUnion([Q1]), "depth" : 25.4 * mm});
        }
        {
            var Q0;
            Q0=makeQuery(id+"F19.boolean.opBoolean","MERGE",FACE,{"derivedFrom":[makeQuery(id+"F17.boolean.opBoolean","MERGE",FACE,{"derivedFrom":[makeQuery(id+"F1.opExtrude","SWEPT_FACE",FACE,{"disambiguationData":[OSD([sQuery(id+"F0.wireOp",EDGE,"E4")])]}),makeQuery(id+"F17.opExtrude","CAP_FACE",FACE,{"disambiguationData":[OSD([sQuery(id+"F16.wireOp",EDGE,"E27.bottom"),sQuery(id+"F16.wireOp",EDGE,"E27.top"),sQuery(id+"F16.wireOp",EDGE,"E27.left"),sQuery(id+"F16.wireOp",EDGE,"E27.right")])],"isStart":true}),makeQuery(id+"F17.opExtrude","CAP_FACE",FACE,{"disambiguationData":[OSD([sQuery(id+"F16.wireOp",EDGE,"E28.bottom"),sQuery(id+"F16.wireOp",EDGE,"E28.top"),sQuery(id+"F16.wireOp",EDGE,"E28.left"),sQuery(id+"F16.wireOp",EDGE,"E28.right")])],"isStart":true}),makeQuery(id+"F17.opExtrude","CAP_FACE",FACE,{"disambiguationData":[OSD([sQuery(id+"F16.wireOp",EDGE,"E29.bottom"),sQuery(id+"F16.wireOp",EDGE,"E29.top"),sQuery(id+"F16.wireOp",EDGE,"E29.left"),sQuery(id+"F16.wireOp",EDGE,"E29.right")])],"isStart":true}),makeQuery(id+"F17.opExtrude","CAP_FACE",FACE,{"disambiguationData":[OSD([sQuery(id+"F16.wireOp",EDGE,"E30.bottom"),sQuery(id+"F16.wireOp",EDGE,"E30.top"),sQuery(id+"F16.wireOp",EDGE,"E30.left"),sQuery(id+"F16.wireOp",EDGE,"E30.right")])],"isStart":true})]}),makeQuery(id+"F19.opExtrude","CAP_FACE",FACE,{"disambiguationData":[OSD([sQuery(id+"F18.wireOp",EDGE,"E31.bottom"),sQuery(id+"F18.wireOp",EDGE,"E31.top"),sQuery(id+"F18.wireOp",EDGE,"E31.left"),sQuery(id+"F18.wireOp",EDGE,"E31.right")])],"isStart":true}),makeQuery(id+"F19.opExtrude","CAP_FACE",FACE,{"disambiguationData":[OSD([sQuery(id+"F18.wireOp",EDGE,"E32.0.1.0"),sQuery(id+"F18.wireOp",EDGE,"E32.0.1.1"),sQuery(id+"F18.wireOp",EDGE,"E32.0.1.2"),sQuery(id+"F18.wireOp",EDGE,"E32.0.1.3")])],"isStart":true}),makeQuery(id+"F19.opExtrude","CAP_FACE",FACE,{"disambiguationData":[OSD([sQuery(id+"F18.wireOp",EDGE,"E32.0.2.0"),sQuery(id+"F18.wireOp",EDGE,"E32.0.2.1"),sQuery(id+"F18.wireOp",EDGE,"E32.0.2.2"),sQuery(id+"F18.wireOp",EDGE,"E32.0.2.3")])],"isStart":true}),makeQuery(id+"F19.opExtrude","CAP_FACE",FACE,{"disambiguationData":[OSD([sQuery(id+"F18.wireOp",EDGE,"E32.0.3.0"),sQuery(id+"F18.wireOp",EDGE,"E32.0.3.1"),sQuery(id+"F18.wireOp",EDGE,"E32.0.3.2"),sQuery(id+"F18.wireOp",EDGE,"E32.0.3.3")])],"isStart":true}),makeQuery(id+"F19.opExtrude","CAP_FACE",FACE,{"disambiguationData":[OSD([sQuery(id+"F18.wireOp",EDGE,"E32.0.4.0"),sQuery(id+"F18.wireOp",EDGE,"E32.0.4.1"),sQuery(id+"F18.wireOp",EDGE,"E32.0.4.2"),sQuery(id+"F18.wireOp",EDGE,"E32.0.4.3")])],"isStart":true}),makeQuery(id+"F19.opExtrude","CAP_FACE",FACE,{"disambiguationData":[OSD([sQuery(id+"F18.wireOp",EDGE,"E32.0.5.0"),sQuery(id+"F18.wireOp",EDGE,"E32.0.5.1"),sQuery(id+"F18.wireOp",EDGE,"E32.0.5.2"),sQuery(id+"F18.wireOp",EDGE,"E32.0.5.3")])],"isStart":true}),makeQuery(id+"F19.opExtrude","CAP_FACE",FACE,{"disambiguationData":[OSD([sQuery(id+"F18.wireOp",EDGE,"E32.0.6.0"),sQuery(id+"F18.wireOp",EDGE,"E32.0.6.1"),sQuery(id+"F18.wireOp",EDGE,"E32.0.6.2"),sQuery(id+"F18.wireOp",EDGE,"E32.0.6.3")])],"isStart":true}),makeQuery(id+"F19.opExtrude","CAP_FACE",FACE,{"disambiguationData":[OSD([sQuery(id+"F18.wireOp",EDGE,"E32.0.7.0"),sQuery(id+"F18.wireOp",EDGE,"E32.0.7.1"),sQuery(id+"F18.wireOp",EDGE,"E32.0.7.2"),sQuery(id+"F18.wireOp",EDGE,"E32.0.7.3")])],"isStart":true}),makeQuery(id+"F19.opExtrude","CAP_FACE",FACE,{"disambiguationData":[OSD([sQuery(id+"F18.wireOp",EDGE,"E32.0.8.0"),sQuery(id+"F18.wireOp",EDGE,"E32.0.8.1"),sQuery(id+"F18.wireOp",EDGE,"E32.0.8.2"),sQuery(id+"F18.wireOp",EDGE,"E32.0.8.3")])],"isStart":true}),makeQuery(id+"F19.opExtrude","CAP_FACE",FACE,{"disambiguationData":[OSD([sQuery(id+"F18.wireOp",EDGE,"E32.0.9.0"),sQuery(id+"F18.wireOp",EDGE,"E32.0.9.1"),sQuery(id+"F18.wireOp",EDGE,"E32.0.9.2"),sQuery(id+"F18.wireOp",EDGE,"E32.0.9.3")])],"isStart":true}),makeQuery(id+"F19.opExtrude","CAP_FACE",FACE,{"disambiguationData":[OSD([sQuery(id+"F18.wireOp",EDGE,"E32.0.10.0"),sQuery(id+"F18.wireOp",EDGE,"E32.0.10.1"),sQuery(id+"F18.wireOp",EDGE,"E32.0.10.2"),sQuery(id+"F18.wireOp",EDGE,"E32.0.10.3")])],"isStart":true}),makeQuery(id+"F19.opExtrude","CAP_FACE",FACE,{"disambiguationData":[OSD([sQuery(id+"F18.wireOp",EDGE,"E32.0.11.0"),sQuery(id+"F18.wireOp",EDGE,"E32.0.11.1"),sQuery(id+"F18.wireOp",EDGE,"E32.0.11.2"),sQuery(id+"F18.wireOp",EDGE,"E32.0.11.3")])],"isStart":true}),makeQuery(id+"F19.opExtrude","CAP_FACE",FACE,{"disambiguationData":[OSD([sQuery(id+"F18.wireOp",EDGE,"E32.1.0.0"),sQuery(id+"F18.wireOp",EDGE,"E32.1.0.1"),sQuery(id+"F18.wireOp",EDGE,"E32.1.0.2"),sQuery(id+"F18.wireOp",EDGE,"E32.1.0.3")])],"isStart":true}),makeQuery(id+"F19.opExtrude","CAP_FACE",FACE,{"disambiguationData":[OSD([sQuery(id+"F18.wireOp",EDGE,"E32.1.1.0"),sQuery(id+"F18.wireOp",EDGE,"E32.1.1.1"),sQuery(id+"F18.wireOp",EDGE,"E32.1.1.2"),sQuery(id+"F18.wireOp",EDGE,"E32.1.1.3")])],"isStart":true}),makeQuery(id+"F19.opExtrude","CAP_FACE",FACE,{"disambiguationData":[OSD([sQuery(id+"F18.wireOp",EDGE,"E32.1.2.0"),sQuery(id+"F18.wireOp",EDGE,"E32.1.2.1"),sQuery(id+"F18.wireOp",EDGE,"E32.1.2.2"),sQuery(id+"F18.wireOp",EDGE,"E32.1.2.3")])],"isStart":true}),makeQuery(id+"F19.opExtrude","CAP_FACE",FACE,{"disambiguationData":[OSD([sQuery(id+"F18.wireOp",EDGE,"E32.1.3.0"),sQuery(id+"F18.wireOp",EDGE,"E32.1.3.1"),sQuery(id+"F18.wireOp",EDGE,"E32.1.3.2"),sQuery(id+"F18.wireOp",EDGE,"E32.1.3.3")])],"isStart":true}),makeQuery(id+"F19.opExtrude","CAP_FACE",FACE,{"disambiguationData":[OSD([sQuery(id+"F18.wireOp",EDGE,"E32.1.4.0"),sQuery(id+"F18.wireOp",EDGE,"E32.1.4.1"),sQuery(id+"F18.wireOp",EDGE,"E32.1.4.2"),sQuery(id+"F18.wireOp",EDGE,"E32.1.4.3")])],"isStart":true}),makeQuery(id+"F19.opExtrude","CAP_FACE",FACE,{"disambiguationData":[OSD([sQuery(id+"F18.wireOp",EDGE,"E32.1.5.0"),sQuery(id+"F18.wireOp",EDGE,"E32.1.5.1"),sQuery(id+"F18.wireOp",EDGE,"E32.1.5.2"),sQuery(id+"F18.wireOp",EDGE,"E32.1.5.3")])],"isStart":true}),makeQuery(id+"F19.opExtrude","CAP_FACE",FACE,{"disambiguationData":[OSD([sQuery(id+"F18.wireOp",EDGE,"E32.1.6.0"),sQuery(id+"F18.wireOp",EDGE,"E32.1.6.1"),sQuery(id+"F18.wireOp",EDGE,"E32.1.6.2"),sQuery(id+"F18.wireOp",EDGE,"E32.1.6.3")])],"isStart":true}),makeQuery(id+"F19.opExtrude","CAP_FACE",FACE,{"disambiguationData":[OSD([sQuery(id+"F18.wireOp",EDGE,"E32.1.7.0"),sQuery(id+"F18.wireOp",EDGE,"E32.1.7.1"),sQuery(id+"F18.wireOp",EDGE,"E32.1.7.2"),sQuery(id+"F18.wireOp",EDGE,"E32.1.7.3")])],"isStart":true}),makeQuery(id+"F19.opExtrude","CAP_FACE",FACE,{"disambiguationData":[OSD([sQuery(id+"F18.wireOp",EDGE,"E32.1.8.0"),sQuery(id+"F18.wireOp",EDGE,"E32.1.8.1"),sQuery(id+"F18.wireOp",EDGE,"E32.1.8.2"),sQuery(id+"F18.wireOp",EDGE,"E32.1.8.3")])],"isStart":true}),makeQuery(id+"F19.opExtrude","CAP_FACE",FACE,{"disambiguationData":[OSD([sQuery(id+"F18.wireOp",EDGE,"E32.1.9.0"),sQuery(id+"F18.wireOp",EDGE,"E32.1.9.1"),sQuery(id+"F18.wireOp",EDGE,"E32.1.9.2"),sQuery(id+"F18.wireOp",EDGE,"E32.1.9.3")])],"isStart":true}),makeQuery(id+"F19.opExtrude","CAP_FACE",FACE,{"disambiguationData":[OSD([sQuery(id+"F18.wireOp",EDGE,"E32.1.10.0"),sQuery(id+"F18.wireOp",EDGE,"E32.1.10.1"),sQuery(id+"F18.wireOp",EDGE,"E32.1.10.2"),sQuery(id+"F18.wireOp",EDGE,"E32.1.10.3")])],"isStart":true}),makeQuery(id+"F19.opExtrude","CAP_FACE",FACE,{"disambiguationData":[OSD([sQuery(id+"F18.wireOp",EDGE,"E32.1.11.0"),sQuery(id+"F18.wireOp",EDGE,"E32.1.11.1"),sQuery(id+"F18.wireOp",EDGE,"E32.1.11.2"),sQuery(id+"F18.wireOp",EDGE,"E32.1.11.3")])],"isStart":true})]});
            var sketch = newSketch(context, id + "F20", { "sketchPlane" : qUnion([Q0])});
            skLineSegment(sketch, "E33.bottom", {"start": v(403.86, -88.9) * mm, "end": v(454.66, -88.9) * mm});
            skLineSegment(sketch, "E33.top", {"start": v(403.86, -66.04) * mm, "end": v(454.66, -66.04) * mm});
            skLineSegment(sketch, "E33.left", {"start": v(403.86, -88.9) * mm, "end": v(403.86, -66.04) * mm});
            skLineSegment(sketch, "E33.right", {"start": v(454.66, -88.9) * mm, "end": v(454.66, -66.04) * mm});
            skLineSegment(sketch, "E34.1.0.0", {"start": v(607.06, -88.9) * mm, "end": v(607.06, -66.04) * mm});
            skLineSegment(sketch, "E34.1.0.1", {"start": v(657.86, -88.9) * mm, "end": v(657.86, -66.04) * mm});
            skLineSegment(sketch, "E34.1.0.2", {"start": v(607.06, -88.9) * mm, "end": v(657.86, -88.9) * mm});
            skLineSegment(sketch, "E34.1.0.3", {"start": v(607.06, -66.04) * mm, "end": v(657.86, -66.04) * mm});
            skLineSegment(sketch, "E34.2.0.0", {"start": v(810.26, -88.9) * mm, "end": v(810.26, -66.04) * mm});
            skLineSegment(sketch, "E34.2.0.1", {"start": v(861.06, -88.9) * mm, "end": v(861.06, -66.04) * mm});
            skLineSegment(sketch, "E34.2.0.2", {"start": v(810.26, -88.9) * mm, "end": v(861.06, -88.9) * mm});
            skLineSegment(sketch, "E34.2.0.3", {"start": v(810.26, -66.04) * mm, "end": v(861.06, -66.04) * mm});
            skLineSegment(sketch, "E34.3.0.0", {"start": v(1013.46, -88.9) * mm, "end": v(1013.46, -66.04) * mm});
            skLineSegment(sketch, "E34.3.0.1", {"start": v(1064.26, -88.9) * mm, "end": v(1064.26, -66.04) * mm});
            skLineSegment(sketch, "E34.3.0.2", {"start": v(1013.46, -88.9) * mm, "end": v(1064.26, -88.9) * mm});
            skLineSegment(sketch, "E34.3.0.3", {"start": v(1013.46, -66.04) * mm, "end": v(1064.26, -66.04) * mm});
            skLineSegment(sketch, "E34.4.0.0", {"start": v(1216.66, -88.9) * mm, "end": v(1216.66, -66.04) * mm});
            skLineSegment(sketch, "E34.4.0.1", {"start": v(1267.46, -88.9) * mm, "end": v(1267.46, -66.04) * mm});
            skLineSegment(sketch, "E34.4.0.2", {"start": v(1216.66, -88.9) * mm, "end": v(1267.46, -88.9) * mm});
            skLineSegment(sketch, "E34.4.0.3", {"start": v(1216.66, -66.04) * mm, "end": v(1267.46, -66.04) * mm});
            skLineSegment(sketch, "E34.5.0.0", {"start": v(1419.86, -88.9) * mm, "end": v(1419.86, -66.04) * mm});
            skLineSegment(sketch, "E34.5.0.1", {"start": v(1470.66, -88.9) * mm, "end": v(1470.66, -66.04) * mm});
            skLineSegment(sketch, "E34.5.0.2", {"start": v(1419.86, -88.9) * mm, "end": v(1470.66, -88.9) * mm});
            skLineSegment(sketch, "E34.5.0.3", {"start": v(1419.86, -66.04) * mm, "end": v(1470.66, -66.04) * mm});
            skLineSegment(sketch, "E34.direction1", {"start": v(403.86, -88.9) * mm, "end": v(607.06, -88.9) * mm, "construction": true});
            skLineSegment(sketch, "E35", {"start": v(127, -1803.4) * mm, "end": v(528.6, -1803.4) * mm});
            skLineSegment(sketch, "E36.MirrorCS", {"start": v(607.06, -3517.9) * mm, "end": v(607.06, -3540.76) * mm});
            skLineSegment(sketch, "E37.MirrorCS", {"start": v(403.86, -3517.9) * mm, "end": v(454.66, -3517.9) * mm});
            skLineSegment(sketch, "E38.MirrorCS", {"start": v(657.86, -3517.9) * mm, "end": v(657.86, -3540.76) * mm});
            skLineSegment(sketch, "E39.MirrorCS", {"start": v(1419.86, -3517.9) * mm, "end": v(1419.86, -3540.76) * mm});
            skLineSegment(sketch, "E40.MirrorCS", {"start": v(810.26, -3517.9) * mm, "end": v(810.26, -3540.76) * mm});
            skLineSegment(sketch, "E41.MirrorCS", {"start": v(454.66, -3517.9) * mm, "end": v(454.66, -3540.76) * mm});
            skLineSegment(sketch, "E42.MirrorCS", {"start": v(1470.66, -3517.9) * mm, "end": v(1470.66, -3540.76) * mm});
            skLineSegment(sketch, "E43.MirrorCS", {"start": v(861.06, -3517.9) * mm, "end": v(861.06, -3540.76) * mm});
            skLineSegment(sketch, "E44.MirrorCS", {"start": v(607.06, -3517.9) * mm, "end": v(657.86, -3517.9) * mm});
            skLineSegment(sketch, "E45.MirrorCS", {"start": v(403.86, -3517.9) * mm, "end": v(403.86, -3540.76) * mm});
            skLineSegment(sketch, "E46.MirrorCS", {"start": v(1267.46, -3517.9) * mm, "end": v(1267.46, -3540.76) * mm});
            skLineSegment(sketch, "E47.MirrorCS", {"start": v(1064.26, -3517.9) * mm, "end": v(1064.26, -3540.76) * mm});
            skLineSegment(sketch, "E48.MirrorCS", {"start": v(607.06, -3540.76) * mm, "end": v(657.86, -3540.76) * mm});
            skLineSegment(sketch, "E49.MirrorCS", {"start": v(403.86, -3540.76) * mm, "end": v(454.66, -3540.76) * mm});
            skLineSegment(sketch, "E50.MirrorCS", {"start": v(403.86, -3517.9) * mm, "end": v(607.06, -3517.9) * mm, "construction": true});
            skLineSegment(sketch, "E51.MirrorCS", {"start": v(810.26, -3540.76) * mm, "end": v(861.06, -3540.76) * mm});
            skLineSegment(sketch, "E52.MirrorCS", {"start": v(1216.66, -3517.9) * mm, "end": v(1216.66, -3540.76) * mm});
            skLineSegment(sketch, "E53.MirrorCS", {"start": v(810.26, -3517.9) * mm, "end": v(861.06, -3517.9) * mm});
            skLineSegment(sketch, "E54.MirrorCS", {"start": v(1216.66, -3517.9) * mm, "end": v(1267.46, -3517.9) * mm});
            skLineSegment(sketch, "E55.MirrorCS", {"start": v(1013.46, -3517.9) * mm, "end": v(1013.46, -3540.76) * mm});
            skLineSegment(sketch, "E56.MirrorCS", {"start": v(1419.86, -3540.76) * mm, "end": v(1470.66, -3540.76) * mm});
            skLineSegment(sketch, "E57.MirrorCS", {"start": v(1216.66, -3540.76) * mm, "end": v(1267.46, -3540.76) * mm});
            skLineSegment(sketch, "E58.MirrorCS", {"start": v(1013.46, -3540.76) * mm, "end": v(1064.26, -3540.76) * mm});
            skLineSegment(sketch, "E59.MirrorCS", {"start": v(1419.86, -3517.9) * mm, "end": v(1470.66, -3517.9) * mm});
            skLineSegment(sketch, "E60.MirrorCS", {"start": v(1013.46, -3517.9) * mm, "end": v(1064.26, -3517.9) * mm});
            skSolve(sketch);
        }
        {
            var Q0;
            Q0 = qSketchRegion(id + "F20", true);
            extrude(context, id + "F21", {"entities" : qUnion([Q0]), "operationType" : NewBodyOperationType.ADD, "endBound" : BoundingType.UP_TO_NEXT, "oppositeDirection" : true, "depth" : 25.4 * mm});
        }
        {
            var Q0;
            {var subQ0=sQuery(id+"F16.wireOp",EDGE,"E30.top");Q0=makeQuery(id+"F19.boolean.opBoolean","SPLIT",FACE,{"disambiguationData":[TD([makeQuery(id+"F17.opExtrude","SWEPT_FACE",FACE,{"disambiguationData":[OSD([subQ0])]})])],"derivedFrom":makeQuery(id+"F3.boolean.opBoolean","COPY",FACE,{"derivedFrom":makeQuery(id+"F3.opExtrude","SWEPT_FACE",FACE,{"disambiguationData":[OSD([sQuery(id+"F2.wireOp",EDGE,"E14.MirrorCS")])]})})});}
            var Q1;
            Q1=makeQuery(id+"F13.boolean.opBoolean","COPY",VERTEX,{"derivedFrom":makeQuery(id+"F13.opExtrude","CAP_VERTEX",VERTEX,{"disambiguationData":[OSD([sQuery(id+"F12.wireOp",EDGE,"E23"),sQuery(id+"F12.wireOp",EDGE,"E24")])],"isStart":false})});
            cPlane(context, id + "F22", {"entities" : qUnion([Q0, Q1]), "cplaneType" : CPlaneType.PLANE_POINT, "offset" : 25.4 * mm, "width" : 152.4 * mm, "height" : 152.4 * mm});
        }
        {
            var Q0;
            Q0=makeQuery(id+"F13.boolean.opBoolean","COPY",FACE,{"derivedFrom":makeQuery(id+"F13.opExtrude","CAP_FACE",FACE,{"disambiguationData":[OSD([sQuery(id+"F0.wireOp",EDGE,"E4"),sQuery(id+"F2.wireOp",EDGE,"E8"),sQuery(id+"F2.wireOp",EDGE,"E14.MirrorCS"),sQuery(id+"F12.wireOp",EDGE,"E22"),sQuery(id+"F12.wireOp",EDGE,"E23"),sQuery(id+"F12.wireOp",EDGE,"E24"),sQuery(id+"F12.wireOp",EDGE,"E25")])],"isStart":false})});
            var sketch = newSketch(context, id + "F23", { "sketchPlane" : qUnion([Q0])});
            skLineSegment(sketch, "E61", {"start": v(1572.26, 4291.62) * mm, "end": v(1572.26, 2362.2) * mm, "construction": true});
            skLineSegment(sketch, "E62.bottom", {"start": v(962.66, 2362.2) * mm, "end": v(2181.86, 2362.2) * mm});
            skLineSegment(sketch, "E62.top", {"start": v(962.66, 203.2) * mm, "end": v(2181.86, 203.2) * mm});
            skLineSegment(sketch, "E62.left", {"start": v(962.66, 2362.2) * mm, "end": v(962.66, 203.2) * mm});
            skLineSegment(sketch, "E62.right", {"start": v(2181.86, 2362.2) * mm, "end": v(2181.86, 203.2) * mm});
            skSolve(sketch);
        }
        {
            var Q0;
            Q0=makeQuery(id+"F23.imprint","IMPRINT",FACE,{"disambiguationData":[TD([[makeQuery(id+"F23.imprint","IMPRINT",EDGE,{"derivedFrom":sQuery(id+"F23.wireOp",EDGE,"E62.bottom")}),-1.0]])]});
            extrude(context, id + "F24", {"entities" : qUnion([Q0]), "operationType" : NewBodyOperationType.ADD, "depth" : 25.4 * mm});
        }
        {
            var Q0;
            Q0=makeQuery(id+"F13.boolean.opBoolean","COPY",VERTEX,{"derivedFrom":makeQuery(id+"F13.opExtrude","CAP_VERTEX",VERTEX,{"disambiguationData":[OSD([sQuery(id+"F12.wireOp",EDGE,"E23"),sQuery(id+"F12.wireOp",EDGE,"E24")])],"isStart":true})});
            var Q1;
            {var subQ1=sQuery(id+"F16.wireOp",EDGE,"E27.top");Q1=makeQuery(id+"F19.boolean.opBoolean","SPLIT",FACE,{"disambiguationData":[TD([makeQuery(id+"F17.opExtrude","SWEPT_FACE",FACE,{"disambiguationData":[OSD([subQ1])]})])],"derivedFrom":makeQuery(id+"F3.boolean.opBoolean","COPY",FACE,{"derivedFrom":makeQuery(id+"F3.opExtrude","SWEPT_FACE",FACE,{"disambiguationData":[OSD([sQuery(id+"F2.wireOp",EDGE,"E8")])]})})});}
            cPlane(context, id + "F25", {"entities" : qUnion([Q0, Q1]), "cplaneType" : CPlaneType.PLANE_POINT, "offset" : 25.4 * mm, "width" : 152.4 * mm, "height" : 152.4 * mm});
        }
        {
            var Q0;
            Q0=qCreatedBy(id+"F25.planeOp",FACE);
            var sketch = newSketch(context, id + "F26", { "sketchPlane" : qUnion([Q0])});
            skLineSegment(sketch, "E63", {"start": v(-88.9, 203.2) * mm, "end": v(5389.98, -83.94) * mm});
            skLineSegment(sketch, "E64", {"start": v(5389.98, -83.94) * mm, "end": v(5389.98, -338.28) * mm});
            skLineSegment(sketch, "E65", {"start": v(5389.98, -338.28) * mm, "end": v(-88.9, -51.15) * mm});
            skLineSegment(sketch, "E66", {"start": v(-88.9, -51.15) * mm, "end": v(-88.9, 203.2) * mm});
            skSolve(sketch);
        }
        {
            var Q0;
            Q0 = qSketchRegion(id + "F26", true);
            extrude(context, id + "F27", {"entities" : qUnion([Q0]), "operationType" : NewBodyOperationType.ADD, "endBound" : BoundingType.SYMMETRIC, "depth" : 1219.2 * mm});
        }
        {
            var Q0;
            Q0=makeQuery(id+"F27.opExtrude","SWEPT_FACE",FACE,{"disambiguationData":[OSD([sQuery(id+"F26.wireOp",EDGE,"E63")])]});
            var sketch = newSketch(context, id + "F28", { "sketchPlane" : qUnion([Q0])});
            skLineSegment(sketch, "E67.bottom", {"start": v(962.66, 99.41) * mm, "end": v(988.06, 99.41) * mm});
            skLineSegment(sketch, "E67.top", {"start": v(962.66, -5490) * mm, "end": v(988.06, -5490) * mm});
            skLineSegment(sketch, "E67.left", {"start": v(962.66, 99.41) * mm, "end": v(962.66, -5490) * mm});
            skLineSegment(sketch, "E67.right", {"start": v(988.06, 99.41) * mm, "end": v(988.06, -5490) * mm});
            skLineSegment(sketch, "E68.bottom", {"start": v(2181.86, 99.41) * mm, "end": v(2156.46, 99.41) * mm});
            skLineSegment(sketch, "E68.top", {"start": v(2181.86, -5479.29) * mm, "end": v(2156.46, -5479.29) * mm});
            skLineSegment(sketch, "E68.left", {"start": v(2181.86, 99.41) * mm, "end": v(2181.86, -5479.29) * mm});
            skLineSegment(sketch, "E68.right", {"start": v(2156.46, 99.41) * mm, "end": v(2156.46, -5479.29) * mm});
            skSolve(sketch);
        }
        {
            var Q0;
            {var subQ0=sQuery(id+"F28.wireOp",EDGE,"E67.right");Q0=makeQuery(id+"F28.imprint","IMPRINT",FACE,{"disambiguationData":[TD([[makeQuery(id+"F28.imprint","IMPRINT",EDGE,{"derivedFrom":subQ0}),1.0]])]});}
            var Q1;
            Q1=makeQuery(id+"F27.opExtrude","SWEPT_FACE",FACE,{"disambiguationData":[OSD([sQuery(id+"F26.wireOp",EDGE,"E64")])]});
            extrude(context, id + "F29", {"entities" : qUnion([Q0, Q1]), "operationType" : NewBodyOperationType.REMOVE, "oppositeDirection" : true, "depth" : 76.2 * mm});
        }
        {
            var Q0;
            Q0=makeQuery(id+"F17.boolean.opBoolean","MERGE",FACE,{"derivedFrom":[makeQuery(id+"F1.opExtrude","SWEPT_FACE",FACE,{"disambiguationData":[OSD([sQuery(id+"F0.wireOp",EDGE,"E4")])]}),makeQuery(id+"F17.opExtrude","CAP_FACE",FACE,{"disambiguationData":[OSD([sQuery(id+"F16.wireOp",EDGE,"E27.bottom"),sQuery(id+"F16.wireOp",EDGE,"E27.top"),sQuery(id+"F16.wireOp",EDGE,"E27.left"),sQuery(id+"F16.wireOp",EDGE,"E27.right")])],"isStart":true}),makeQuery(id+"F17.opExtrude","CAP_FACE",FACE,{"disambiguationData":[OSD([sQuery(id+"F16.wireOp",EDGE,"E28.bottom"),sQuery(id+"F16.wireOp",EDGE,"E28.top"),sQuery(id+"F16.wireOp",EDGE,"E28.left"),sQuery(id+"F16.wireOp",EDGE,"E28.right")])],"isStart":true}),makeQuery(id+"F17.opExtrude","CAP_FACE",FACE,{"disambiguationData":[OSD([sQuery(id+"F16.wireOp",EDGE,"E29.bottom"),sQuery(id+"F16.wireOp",EDGE,"E29.top"),sQuery(id+"F16.wireOp",EDGE,"E29.left"),sQuery(id+"F16.wireOp",EDGE,"E29.right")])],"isStart":true}),makeQuery(id+"F17.opExtrude","CAP_FACE",FACE,{"disambiguationData":[OSD([sQuery(id+"F16.wireOp",EDGE,"E30.bottom"),sQuery(id+"F16.wireOp",EDGE,"E30.top"),sQuery(id+"F16.wireOp",EDGE,"E30.left"),sQuery(id+"F16.wireOp",EDGE,"E30.right")])],"isStart":true})]});
            var sketch = newSketch(context, id + "F30", { "sketchPlane" : qUnion([Q0])});
            skCircle(sketch, "E69.cCircle", {"center": v(203.2, -165.1) * mm, "radius": 101.6 * mm, "construction": true});
            skLineSegment(sketch, "E69.0", {"start": v(311.78, -182.5) * mm, "end": v(267.67, -254.19) * mm});
            skLineSegment(sketch, "E69.1", {"start": v(267.67, -254.19) * mm, "end": v(185.8, -273.68) * mm});
            skLineSegment(sketch, "E69.2", {"start": v(185.8, -273.68) * mm, "end": v(114.11, -229.57) * mm});
            skLineSegment(sketch, "E69.3", {"start": v(114.11, -229.57) * mm, "end": v(94.62, -147.7) * mm});
            skLineSegment(sketch, "E69.4", {"start": v(94.62, -147.7) * mm, "end": v(138.73, -76.01) * mm});
            skLineSegment(sketch, "E69.5", {"start": v(138.73, -76.01) * mm, "end": v(220.6, -56.52) * mm});
            skLineSegment(sketch, "E69.6", {"start": v(220.6, -56.52) * mm, "end": v(292.29, -100.63) * mm});
            skLineSegment(sketch, "E69.7", {"start": v(292.29, -100.63) * mm, "end": v(311.78, -182.5) * mm});
            skPoint(sketch, "E69.0.midPoint", {"position": v(289.73, -218.35) * mm});
            skLineSegment(sketch, "E70.MirrorCS", {"start": v(1572.26, -88.9) * mm, "end": v(1572.26, -695.32) * mm, "construction": true});
            skLineSegment(sketch, "E71", {"start": v(0, -1803.4) * mm, "end": v(1462.96, -1803.4) * mm, "construction": true});
            skLineSegment(sketch, "E72.MirrorCS", {"start": v(2958.73, -273.68) * mm, "end": v(3030.4, -229.57) * mm});
            skLineSegment(sketch, "E73.MirrorCS", {"start": v(2832.74, -182.5) * mm, "end": v(2876.85, -254.19) * mm});
            skLineSegment(sketch, "E74.MirrorCS", {"start": v(3005.8, -76.01) * mm, "end": v(2923.91, -56.52) * mm});
            skLineSegment(sketch, "E75.MirrorCS", {"start": v(3030.4, -229.57) * mm, "end": v(3049.9, -147.7) * mm});
            skLineSegment(sketch, "E76.MirrorCS", {"start": v(3049.9, -147.7) * mm, "end": v(3005.8, -76.01) * mm});
            skPoint(sketch, "E77.MirrorP", {"position": v(2854.8, -218.35) * mm});
            skLineSegment(sketch, "E78.MirrorCS", {"start": v(2876.85, -254.19) * mm, "end": v(2958.73, -273.68) * mm});
            skLineSegment(sketch, "E79.MirrorCS", {"start": v(2923.91, -56.52) * mm, "end": v(2852.23, -100.63) * mm});
            skCircle(sketch, "E80.MirrorC", {"center": v(2941.32, -165.1) * mm, "radius": 101.6 * mm, "construction": true});
            skLineSegment(sketch, "E81.MirrorCS", {"start": v(2852.23, -100.63) * mm, "end": v(2832.74, -182.5) * mm});
            skLineSegment(sketch, "E82.MirrorCS", {"start": v(185.8, -3333.12) * mm, "end": v(114.11, -3377.23) * mm});
            skLineSegment(sketch, "E83.MirrorCS", {"start": v(311.78, -3424.3) * mm, "end": v(267.67, -3352.61) * mm});
            skPoint(sketch, "E84.MirrorP", {"position": v(289.73, -3388.45) * mm});
            skCircle(sketch, "E85.MirrorC", {"center": v(203.2, -3441.7) * mm, "radius": 101.6 * mm, "construction": true});
            skLineSegment(sketch, "E86.MirrorCS", {"start": v(114.11, -3377.23) * mm, "end": v(94.62, -3459.1) * mm});
            skLineSegment(sketch, "E87.MirrorCS", {"start": v(138.73, -3530.79) * mm, "end": v(220.6, -3550.28) * mm});
            skLineSegment(sketch, "E88.MirrorCS", {"start": v(292.29, -3506.17) * mm, "end": v(311.78, -3424.3) * mm});
            skLineSegment(sketch, "E89.MirrorCS", {"start": v(267.67, -3352.61) * mm, "end": v(185.8, -3333.12) * mm});
            skLineSegment(sketch, "E90.MirrorCS", {"start": v(94.62, -3459.1) * mm, "end": v(138.73, -3530.79) * mm});
            skLineSegment(sketch, "E91.MirrorCS", {"start": v(220.6, -3550.28) * mm, "end": v(292.29, -3506.17) * mm});
            skLineSegment(sketch, "E92.MirrorCS", {"start": v(2832.74, -3424.3) * mm, "end": v(2876.85, -3352.61) * mm});
            skLineSegment(sketch, "E93.MirrorCS", {"start": v(2958.73, -3333.12) * mm, "end": v(3030.4, -3377.23) * mm});
            skLineSegment(sketch, "E94.MirrorCS", {"start": v(3049.9, -3459.1) * mm, "end": v(3005.8, -3530.79) * mm});
            skLineSegment(sketch, "E95.MirrorCS", {"start": v(2852.23, -3506.17) * mm, "end": v(2832.74, -3424.3) * mm});
            skLineSegment(sketch, "E96.MirrorCS", {"start": v(2923.91, -3550.28) * mm, "end": v(2852.23, -3506.17) * mm});
            skLineSegment(sketch, "E97.MirrorCS", {"start": v(2876.85, -3352.61) * mm, "end": v(2958.73, -3333.12) * mm});
            skPoint(sketch, "E98.MirrorP", {"position": v(2854.8, -3388.45) * mm});
            skLineSegment(sketch, "E99.MirrorCS", {"start": v(3030.4, -3377.23) * mm, "end": v(3049.9, -3459.1) * mm});
            skLineSegment(sketch, "E100.MirrorCS", {"start": v(3005.8, -3530.79) * mm, "end": v(2923.91, -3550.28) * mm});
            skCircle(sketch, "E101.MirrorC", {"center": v(2941.32, -3441.7) * mm, "radius": 101.6 * mm, "construction": true});
            skSolve(sketch);
        }
        {
            var Q0;
            Q0 = qSketchRegion(id + "F30", true);
            extrude(context, id + "F31", {"entities" : qUnion([Q0]), "operationType" : NewBodyOperationType.ADD, "depth" : 635 * mm});
        }
        {
            var Q0;
            {var subQ1=sQuery(id+"F18.wireOp",EDGE,"E32.0.5.2");Q0=makeQuery(id+"F19.boolean.opBoolean","SPLIT",FACE,{"disambiguationData":[TD([makeQuery(id+"F19.opExtrude","SWEPT_FACE",FACE,{"disambiguationData":[OSD([subQ1])]})])],"derivedFrom":makeQuery(id+"F3.boolean.opBoolean","COPY",FACE,{"derivedFrom":makeQuery(id+"F3.opExtrude","SWEPT_FACE",FACE,{"disambiguationData":[OSD([sQuery(id+"F2.wireOp",EDGE,"E8")])]})})});}
            var sketch = newSketch(context, id + "F32", { "sketchPlane" : qUnion([Q0])});
            skLineSegment(sketch, "E102.bottom", {"start": v(-2006.6, 1828.8) * mm, "end": v(-1346.2, 1828.8) * mm});
            skLineSegment(sketch, "E102.top", {"start": v(-2006.6, 914.4) * mm, "end": v(-1346.2, 914.4) * mm});
            skLineSegment(sketch, "E102.left", {"start": v(-2006.6, 1828.8) * mm, "end": v(-2006.6, 914.4) * mm});
            skLineSegment(sketch, "E102.right", {"start": v(-1346.2, 1828.8) * mm, "end": v(-1346.2, 914.4) * mm});
            skSolve(sketch);
        }
        {
            var Q0;
            Q0 = qSketchRegion(id + "F32", true);
            extrude(context, id + "F33", {"entities" : qUnion([Q0]), "operationType" : NewBodyOperationType.ADD, "depth" : 25.4 * mm});
        }
        {
            var Q0;
            {var subQ0=sQuery(id+"F18.wireOp",EDGE,"E32.1.6.2");Q0=makeQuery(id+"F19.boolean.opBoolean","SPLIT",FACE,{"disambiguationData":[TD([makeQuery(id+"F19.opExtrude","SWEPT_FACE",FACE,{"disambiguationData":[OSD([subQ0])]})])],"derivedFrom":makeQuery(id+"F3.boolean.opBoolean","COPY",FACE,{"derivedFrom":makeQuery(id+"F3.opExtrude","SWEPT_FACE",FACE,{"disambiguationData":[OSD([sQuery(id+"F2.wireOp",EDGE,"E14.MirrorCS")])]})})});}
            var sketch = newSketch(context, id + "F34", { "sketchPlane" : qUnion([Q0])});
            skLineSegment(sketch, "E103.0.0", {"start": v(1346.2, 1828.8) * mm, "end": v(2006.6, 1828.8) * mm});
            skLineSegment(sketch, "E103.0.1", {"start": v(2006.6, 1828.8) * mm, "end": v(2006.6, 914.4) * mm});
            skLineSegment(sketch, "E103.0.2", {"start": v(2006.6, 914.4) * mm, "end": v(1346.2, 914.4) * mm});
            skLineSegment(sketch, "E103.0.3", {"start": v(1346.2, 914.4) * mm, "end": v(1346.2, 1828.8) * mm});
            skSolve(sketch);
        }
        {
            var Q0;
            Q0 = qSketchRegion(id + "F34", true);
            extrude(context, id + "F35", {"entities" : qUnion([Q0]), "operationType" : NewBodyOperationType.ADD, "depth" : 25.4 * mm});
        }
        {
            var Q0;
            Q0=makeQuery(id+"F35.opExtrude","CAP_FACE",FACE,{"disambiguationData":[OSD([sQuery(id+"F34.wireOp",EDGE,"E103.0.0"),sQuery(id+"F34.wireOp",EDGE,"E103.0.1"),sQuery(id+"F34.wireOp",EDGE,"E103.0.2"),sQuery(id+"F34.wireOp",EDGE,"E103.0.3")])],"isStart":false});
            var sketch = newSketch(context, id + "F36", { "sketchPlane" : qUnion([Q0])});
            skLineSegment(sketch, "E104.0", {"start": v(1905, 1727.2) * mm, "end": v(1447.8, 1727.2) * mm});
            skLineSegment(sketch, "E104.1", {"start": v(1905, 1016) * mm, "end": v(1905, 1727.2) * mm});
            skLineSegment(sketch, "E104.2", {"start": v(1447.8, 1016) * mm, "end": v(1905, 1016) * mm});
            skLineSegment(sketch, "E104.3", {"start": v(1447.8, 1727.2) * mm, "end": v(1447.8, 1016) * mm});
            skSolve(sketch);
        }
        {
            var Q0;
            Q0 = qSketchRegion(id + "F36", true);
            extrude(context, id + "F37", {"entities" : qUnion([Q0]), "operationType" : NewBodyOperationType.REMOVE, "oppositeDirection" : true, "depth" : 50.8 * mm});
        }
        {
            var Q0;
            Q0=makeQuery(id+"F33.opExtrude","CAP_FACE",FACE,{"disambiguationData":[OSD([sQuery(id+"F32.wireOp",EDGE,"E102.bottom"),sQuery(id+"F32.wireOp",EDGE,"E102.top"),sQuery(id+"F32.wireOp",EDGE,"E102.left"),sQuery(id+"F32.wireOp",EDGE,"E102.right")])],"isStart":false});
            var sketch = newSketch(context, id + "F38", { "sketchPlane" : qUnion([Q0])});
            skLineSegment(sketch, "E105.0", {"start": v(-1447.8, 1727.2) * mm, "end": v(-1905, 1727.2) * mm});
            skLineSegment(sketch, "E105.1", {"start": v(-1447.8, 1016) * mm, "end": v(-1447.8, 1727.2) * mm});
            skLineSegment(sketch, "E105.2", {"start": v(-1905, 1016) * mm, "end": v(-1447.8, 1016) * mm});
            skLineSegment(sketch, "E105.3", {"start": v(-1905, 1727.2) * mm, "end": v(-1905, 1016) * mm});
            skSolve(sketch);
        }
        {
            var Q0;
            Q0 = qSketchRegion(id + "F38", true);
            extrude(context, id + "F39", {"entities" : qUnion([Q0]), "operationType" : NewBodyOperationType.REMOVE, "oppositeDirection" : true, "depth" : 50.8 * mm});
        }
        {
            var Q0;
            {var subQ0=sQuery(id+"F14.wireOp",EDGE,"E26.0.6");var subQ2=sQuery(id+"F20.wireOp",EDGE,"E39.MirrorCS");Q0=makeQuery(id+"F21.boolean.opBoolean","SPLIT",FACE,{"disambiguationData":[TD([makeQuery(id+"F21.opExtrude","SWEPT_FACE",FACE,{"disambiguationData":[OSD([subQ2])]})])],"derivedFrom":makeQuery(id+"F15.boolean.opBoolean","COPY",FACE,{"derivedFrom":makeQuery(id+"F15.opExtrude","CAP_FACE",FACE,{"disambiguationData":[OSD([sQuery(id+"F14.wireOp",EDGE,"E26.0.0"),sQuery(id+"F14.wireOp",EDGE,"E26.0.1"),sQuery(id+"F14.wireOp",EDGE,"E26.0.2"),sQuery(id+"F14.wireOp",EDGE,"E26.0.3"),sQuery(id+"F14.wireOp",EDGE,"E26.0.4"),sQuery(id+"F14.wireOp",EDGE,"E26.0.5"),subQ0])],"isStart":false})})});}
            var sketch = newSketch(context, id + "F40", { "sketchPlane" : qUnion([Q0])});
            skLineSegment(sketch, "E106.bottom", {"start": v(-1978.66, 1828.8) * mm, "end": v(-1165.86, 1828.8) * mm});
            skLineSegment(sketch, "E106.top", {"start": v(-1978.66, 914.4) * mm, "end": v(-1165.86, 914.4) * mm});
            skLineSegment(sketch, "E106.left", {"start": v(-1978.66, 1828.8) * mm, "end": v(-1978.66, 914.4) * mm});
            skLineSegment(sketch, "E106.right", {"start": v(-1165.86, 1828.8) * mm, "end": v(-1165.86, 914.4) * mm});
            skSolve(sketch);
        }
        {
            var Q0;
            Q0 = qSketchRegion(id + "F40", true);
            extrude(context, id + "F41", {"entities" : qUnion([Q0]), "operationType" : NewBodyOperationType.ADD, "depth" : 25.4 * mm});
        }
        {
            var Q0;
            Q0=makeQuery(id+"F41.opExtrude","CAP_FACE",FACE,{"disambiguationData":[OSD([sQuery(id+"F40.wireOp",EDGE,"E106.bottom"),sQuery(id+"F40.wireOp",EDGE,"E106.top"),sQuery(id+"F40.wireOp",EDGE,"E106.left"),sQuery(id+"F40.wireOp",EDGE,"E106.right")])],"isStart":false});
            var sketch = newSketch(context, id + "F42", { "sketchPlane" : qUnion([Q0])});
            skLineSegment(sketch, "E107.0", {"start": v(-1267.46, 1727.2) * mm, "end": v(-1877.06, 1727.2) * mm});
            skLineSegment(sketch, "E107.1", {"start": v(-1267.46, 1016) * mm, "end": v(-1267.46, 1727.2) * mm});
            skLineSegment(sketch, "E107.2", {"start": v(-1877.06, 1016) * mm, "end": v(-1267.46, 1016) * mm});
            skLineSegment(sketch, "E107.3", {"start": v(-1877.06, 1727.2) * mm, "end": v(-1877.06, 1016) * mm});
            skSolve(sketch);
        }
        {
            var Q0;
            Q0 = qSketchRegion(id + "F42", true);
            extrude(context, id + "F43", {"entities" : qUnion([Q0]), "operationType" : NewBodyOperationType.REMOVE, "oppositeDirection" : true, "depth" : 50.8 * mm});
        }
    });
